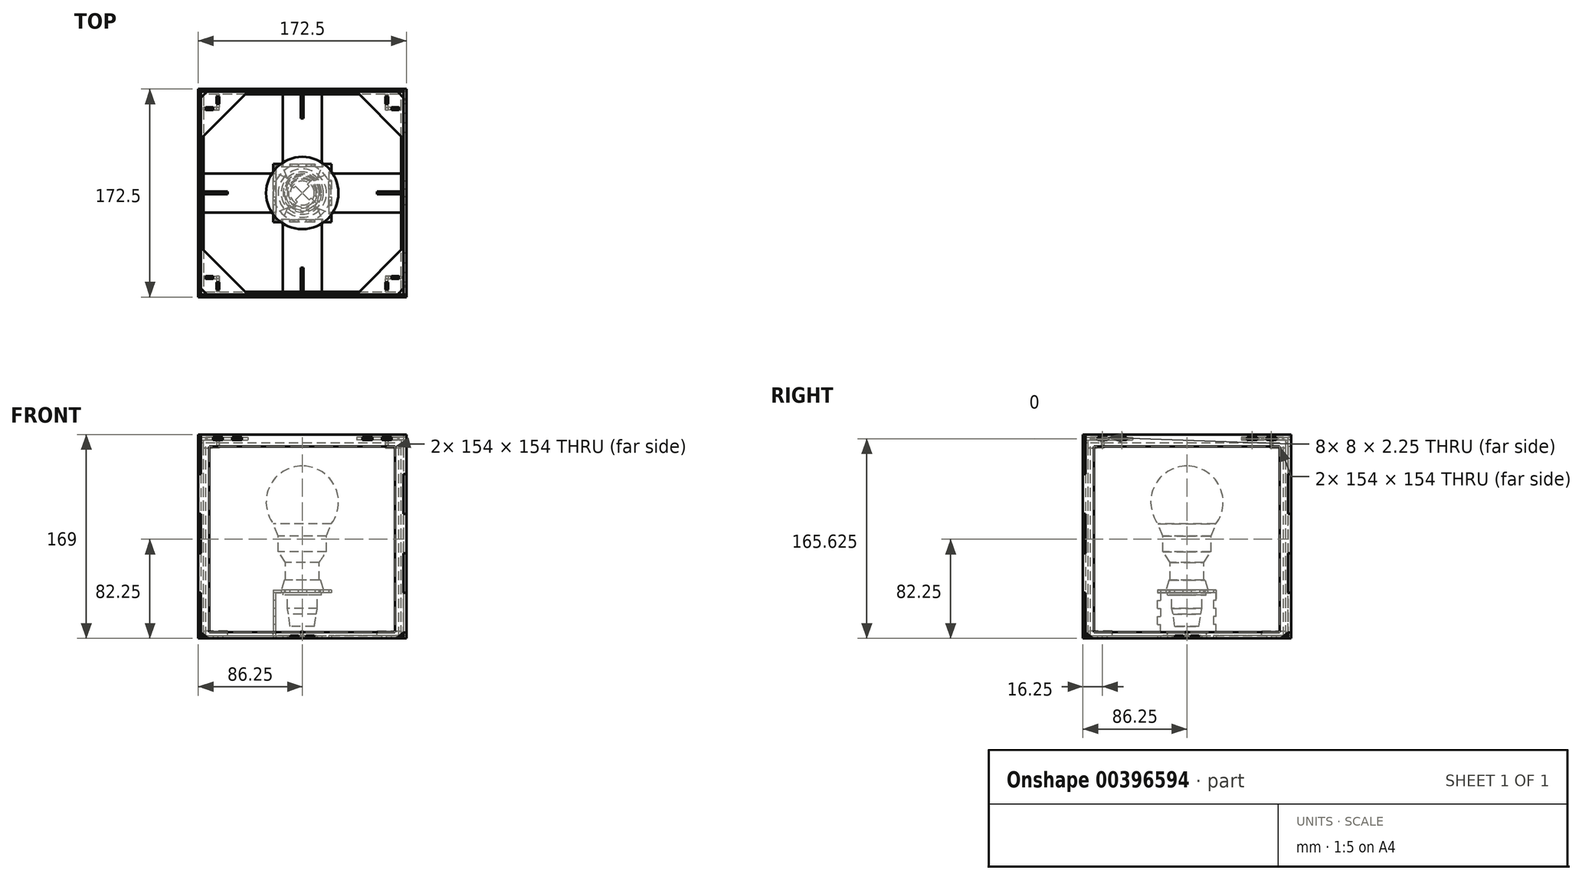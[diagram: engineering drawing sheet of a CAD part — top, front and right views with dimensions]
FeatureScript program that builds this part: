
annotation { "Feature Type Name" : "Feature", "Feature Type Description" : "" }
export const myFeature = defineFeature(function(context is Context, id is Id, definition is map)
    precondition{}
    {
        {
            assignVariable(context, id + "F0", {"name" : "ep", "anyValue" : 2.25});
        }
        {
            var Q0;
            Q0=qCreatedBy(makeId("Front.planeOp"),FACE);
            var sketch = newSketch(context, id + "F1", { "sketchPlane" : qUnion([Q0])});
            skLineSegment(sketch, "E0", {"start": v(0, 10) * mm, "end": v(10, 10) * mm});
            skLineSegment(sketch, "E1", {"start": v(10, 10) * mm, "end": v(11.5, 20) * mm});
            skLineSegment(sketch, "E2", {"start": v(11.5, 20) * mm, "end": v(12.5, 25) * mm});
            skLineSegment(sketch, "E3", {"start": v(12.5, 25) * mm, "end": v(12.5, 36) * mm});
            skLineSegment(sketch, "E4", {"start": v(12.5, 36) * mm, "end": v(16, 36) * mm});
            skLineSegment(sketch, "E5", {"start": v(16, 36) * mm, "end": v(16, 38) * mm});
            skLineSegment(sketch, "E6", {"start": v(16, 38) * mm, "end": v(14, 38) * mm});
            skLineSegment(sketch, "E7", {"start": v(14, 38) * mm, "end": v(14, 40.25) * mm});
            skLineSegment(sketch, "E8", {"start": v(14, 40.25) * mm, "end": v(17.5, 40.25) * mm});
            skLineSegment(sketch, "E9", {"start": v(17.5, 40.25) * mm, "end": v(15, 48.25) * mm});
            skLineSegment(sketch, "E10", {"start": v(15, 48.25) * mm, "end": v(14, 48.25) * mm});
            skLineSegment(sketch, "E11", {"start": v(14, 48.25) * mm, "end": v(14, 63) * mm});
            skLineSegment(sketch, "E12", {"start": v(14, 63) * mm, "end": v(20, 72) * mm});
            skLineSegment(sketch, "E13", {"start": v(20, 72) * mm, "end": v(20, 85) * mm});
            skLineSegment(sketch, "E14", {"start": v(20, 85) * mm, "end": v(24, 95) * mm});
            skLineSegment(sketch, "E15", {"start": v(0, 10) * mm, "end": v(0, 113) * mm, "construction": true});
            skArc(sketch, "E16", {"start": v(24, 95) * mm, "mid": v(26.83, 126.42) * mm, "end": v(0, 143) * mm});
            skLineSegment(sketch, "E17", {"start": v(0, 143) * mm, "end": v(0, 10) * mm});
            skSolve(sketch);
        }
        {
            var Q0;
            Q0 = qSketchRegion(id + "F1", true);
            var Q1;
            Q1=sQuery(id+"F1.wireOp",EDGE,"E17");
            revolve(context, id + "F2", {"entities" : qUnion([Q0]), "axis" : qUnion([Q1]), "revolveType" : RevolveType.FULL});
        }
        {
            var Q0;
            Q0=makeQuery(id+"F2.opRevolve","SWEPT_FACE",FACE,{"disambiguationData":[OSD([sQuery(id+"F1.wireOp",EDGE,"E6")])]});
            var sketch = newSketch(context, id + "F3", { "sketchPlane" : qUnion([Q0])});
            skCircle(sketch, "E18.0", {"center": v(0, 0) * mm, "radius": 15 * mm});
            skLineSegment(sketch, "E19.top", {"start": v(-17.32, 22) * mm, "end": v(-10.4, 22) * mm});
            skLineSegment(sketch, "E19.left", {"start": v(-17.32, 24.25) * mm, "end": v(-17.32, 22) * mm});
            skLineSegment(sketch, "E19.right", {"start": v(-10.4, 24.25) * mm, "end": v(-10.4, 22) * mm});
            skLineSegment(sketch, "E20.1.0.0", {"start": v(3.46, 24.25) * mm, "end": v(3.46, 22) * mm});
            skLineSegment(sketch, "E20.1.0.1", {"start": v(-3.46, 22) * mm, "end": v(3.46, 22) * mm});
            skLineSegment(sketch, "E20.1.0.3", {"start": v(-3.46, 24.25) * mm, "end": v(-3.46, 22) * mm});
            skLineSegment(sketch, "E20.2.0.0", {"start": v(17.32, 24.25) * mm, "end": v(17.32, 22) * mm});
            skLineSegment(sketch, "E20.2.0.1", {"start": v(10.4, 22) * mm, "end": v(17.32, 22) * mm});
            skLineSegment(sketch, "E20.2.0.3", {"start": v(10.4, 24.25) * mm, "end": v(10.4, 22) * mm});
            skLineSegment(sketch, "E21", {"start": v(-24.25, 24.25) * mm, "end": v(-17.32, 24.25) * mm});
            skLineSegment(sketch, "E22", {"start": v(-10.4, 24.25) * mm, "end": v(-3.46, 24.25) * mm});
            skLineSegment(sketch, "E23", {"start": v(3.46, 24.25) * mm, "end": v(10.4, 24.25) * mm});
            skLineSegment(sketch, "E24", {"start": v(17.32, 24.25) * mm, "end": v(24.25, 24.25) * mm});
            skLineSegment(sketch, "E25.1.0", {"start": v(-24.25, -3.46) * mm, "end": v(-22, -3.46) * mm});
            skLineSegment(sketch, "E25.1.1", {"start": v(-22, -3.46) * mm, "end": v(-22, 3.46) * mm});
            skLineSegment(sketch, "E25.1.2", {"start": v(-24.25, 17.32) * mm, "end": v(-22, 17.32) * mm});
            skLineSegment(sketch, "E25.1.3", {"start": v(-24.25, 3.46) * mm, "end": v(-24.25, 10.4) * mm});
            skLineSegment(sketch, "E25.1.4", {"start": v(-24.25, 3.46) * mm, "end": v(-22, 3.46) * mm});
            skLineSegment(sketch, "E25.1.5", {"start": v(-24.25, -10.4) * mm, "end": v(-24.25, -3.46) * mm});
            skLineSegment(sketch, "E25.1.6", {"start": v(-24.25, -10.4) * mm, "end": v(-22, -10.4) * mm});
            skLineSegment(sketch, "E25.1.7", {"start": v(-24.25, -24.25) * mm, "end": v(-24.25, -17.32) * mm});
            skLineSegment(sketch, "E25.1.8", {"start": v(-24.25, 10.4) * mm, "end": v(-22, 10.4) * mm});
            skLineSegment(sketch, "E25.1.9", {"start": v(-24.25, -17.32) * mm, "end": v(-22, -17.32) * mm});
            skLineSegment(sketch, "E25.1.10", {"start": v(-22, 10.4) * mm, "end": v(-22, 17.32) * mm});
            skLineSegment(sketch, "E25.1.11", {"start": v(-24.25, 17.32) * mm, "end": v(-24.25, 24.25) * mm});
            skLineSegment(sketch, "E25.1.12", {"start": v(-22, -17.32) * mm, "end": v(-22, -10.4) * mm});
            skLineSegment(sketch, "E25.2.0", {"start": v(3.46, -24.25) * mm, "end": v(3.46, -22) * mm});
            skLineSegment(sketch, "E25.2.1", {"start": v(3.46, -22) * mm, "end": v(-3.46, -22) * mm});
            skLineSegment(sketch, "E25.2.2", {"start": v(-17.32, -24.25) * mm, "end": v(-17.32, -22) * mm});
            skLineSegment(sketch, "E25.2.3", {"start": v(-3.46, -24.25) * mm, "end": v(-10.4, -24.25) * mm});
            skLineSegment(sketch, "E25.2.4", {"start": v(-3.46, -24.25) * mm, "end": v(-3.46, -22) * mm});
            skLineSegment(sketch, "E25.2.5", {"start": v(10.4, -24.25) * mm, "end": v(3.46, -24.25) * mm});
            skLineSegment(sketch, "E25.2.6", {"start": v(10.4, -24.25) * mm, "end": v(10.4, -22) * mm});
            skLineSegment(sketch, "E25.2.7", {"start": v(24.25, -24.25) * mm, "end": v(17.32, -24.25) * mm});
            skLineSegment(sketch, "E25.2.8", {"start": v(-10.4, -24.25) * mm, "end": v(-10.4, -22) * mm});
            skLineSegment(sketch, "E25.2.9", {"start": v(17.32, -24.25) * mm, "end": v(17.32, -22) * mm});
            skLineSegment(sketch, "E25.2.10", {"start": v(-10.4, -22) * mm, "end": v(-17.32, -22) * mm});
            skLineSegment(sketch, "E25.2.11", {"start": v(-17.32, -24.25) * mm, "end": v(-24.25, -24.25) * mm});
            skLineSegment(sketch, "E25.2.12", {"start": v(17.32, -22) * mm, "end": v(10.4, -22) * mm});
            skLineSegment(sketch, "E25.3.0", {"start": v(24.25, 3.46) * mm, "end": v(22, 3.46) * mm});
            skLineSegment(sketch, "E25.3.1", {"start": v(22, 3.46) * mm, "end": v(22, -3.46) * mm});
            skLineSegment(sketch, "E25.3.2", {"start": v(24.25, -17.32) * mm, "end": v(22, -17.32) * mm});
            skLineSegment(sketch, "E25.3.3", {"start": v(24.25, -3.46) * mm, "end": v(24.25, -10.4) * mm});
            skLineSegment(sketch, "E25.3.4", {"start": v(24.25, -3.46) * mm, "end": v(22, -3.46) * mm});
            skLineSegment(sketch, "E25.3.5", {"start": v(24.25, 10.4) * mm, "end": v(24.25, 3.46) * mm});
            skLineSegment(sketch, "E25.3.6", {"start": v(24.25, 10.4) * mm, "end": v(22, 10.4) * mm});
            skLineSegment(sketch, "E25.3.7", {"start": v(24.25, 24.25) * mm, "end": v(24.25, 17.32) * mm});
            skLineSegment(sketch, "E25.3.8", {"start": v(24.25, -10.4) * mm, "end": v(22, -10.4) * mm});
            skLineSegment(sketch, "E25.3.9", {"start": v(24.25, 17.32) * mm, "end": v(22, 17.32) * mm});
            skLineSegment(sketch, "E25.3.10", {"start": v(22, -10.4) * mm, "end": v(22, -17.32) * mm});
            skLineSegment(sketch, "E25.3.11", {"start": v(24.25, -17.32) * mm, "end": v(24.25, -24.25) * mm});
            skLineSegment(sketch, "E25.3.12", {"start": v(22, 17.32) * mm, "end": v(22, 10.4) * mm});
            skSolve(sketch);
        }
        {
            var Q0;
            Q0=makeQuery(id+"F3.imprint","IMPRINT",FACE,{"disambiguationData":[TD([[makeQuery(id+"F3.imprint","IMPRINT",EDGE,{"derivedFrom":sQuery(id+"F3.wireOp",EDGE,"E19.top")}),-1.0]])]});
            var Q1;
            Q1=makeQuery(id+"F3.imprint","IMPRINT",FACE,{"disambiguationData":[TD([[makeQuery(id+"F3.imprint","IMPRINT",EDGE,{"derivedFrom":sQuery(id+"F3.wireOp",EDGE,"E18.0")}),-1.0]])]});
            extrude(context, id + "F4", {"entities" : qUnion([Q0, Q1]), "depth" : (getVariable(context, 'ep')) * mm});
        }
        {
            var Q0;
            Q0=makeQuery(id+"F4.opExtrude","CAP_FACE",FACE,{"disambiguationData":[OSD([sQuery(id+"F3.wireOp",EDGE,"E18.0"),sQuery(id+"F3.wireOp",EDGE,"E19.top"),sQuery(id+"F3.wireOp",EDGE,"E19.left"),sQuery(id+"F3.wireOp",EDGE,"E19.right"),sQuery(id+"F3.wireOp",EDGE,"E20.1.0.0"),sQuery(id+"F3.wireOp",EDGE,"E20.1.0.1"),sQuery(id+"F3.wireOp",EDGE,"E20.1.0.3"),sQuery(id+"F3.wireOp",EDGE,"E20.2.0.0"),sQuery(id+"F3.wireOp",EDGE,"E20.2.0.1"),sQuery(id+"F3.wireOp",EDGE,"E20.2.0.3"),sQuery(id+"F3.wireOp",EDGE,"E21"),sQuery(id+"F3.wireOp",EDGE,"E22"),sQuery(id+"F3.wireOp",EDGE,"E23"),sQuery(id+"F3.wireOp",EDGE,"E24"),sQuery(id+"F3.wireOp",EDGE,"E25.1.0"),sQuery(id+"F3.wireOp",EDGE,"E25.1.1"),sQuery(id+"F3.wireOp",EDGE,"E25.1.2"),sQuery(id+"F3.wireOp",EDGE,"E25.1.3"),sQuery(id+"F3.wireOp",EDGE,"E25.1.4"),sQuery(id+"F3.wireOp",EDGE,"E25.1.5"),sQuery(id+"F3.wireOp",EDGE,"E25.1.6"),sQuery(id+"F3.wireOp",EDGE,"E25.1.7"),sQuery(id+"F3.wireOp",EDGE,"E25.1.8"),sQuery(id+"F3.wireOp",EDGE,"E25.1.9"),sQuery(id+"F3.wireOp",EDGE,"E25.1.10"),sQuery(id+"F3.wireOp",EDGE,"E25.1.11"),sQuery(id+"F3.wireOp",EDGE,"E25.1.12"),sQuery(id+"F3.wireOp",EDGE,"E25.2.0"),sQuery(id+"F3.wireOp",EDGE,"E25.2.1"),sQuery(id+"F3.wireOp",EDGE,"E25.2.2"),sQuery(id+"F3.wireOp",EDGE,"E25.2.3"),sQuery(id+"F3.wireOp",EDGE,"E25.2.4"),sQuery(id+"F3.wireOp",EDGE,"E25.2.5"),sQuery(id+"F3.wireOp",EDGE,"E25.2.6"),sQuery(id+"F3.wireOp",EDGE,"E25.2.7"),sQuery(id+"F3.wireOp",EDGE,"E25.2.8"),sQuery(id+"F3.wireOp",EDGE,"E25.2.9"),sQuery(id+"F3.wireOp",EDGE,"E25.2.10"),sQuery(id+"F3.wireOp",EDGE,"E25.2.11"),sQuery(id+"F3.wireOp",EDGE,"E25.2.12"),sQuery(id+"F3.wireOp",EDGE,"E25.3.0"),sQuery(id+"F3.wireOp",EDGE,"E25.3.1"),sQuery(id+"F3.wireOp",EDGE,"E25.3.2"),sQuery(id+"F3.wireOp",EDGE,"E25.3.3"),sQuery(id+"F3.wireOp",EDGE,"E25.3.4"),sQuery(id+"F3.wireOp",EDGE,"E25.3.5"),sQuery(id+"F3.wireOp",EDGE,"E25.3.6"),sQuery(id+"F3.wireOp",EDGE,"E25.3.7"),sQuery(id+"F3.wireOp",EDGE,"E25.3.8"),sQuery(id+"F3.wireOp",EDGE,"E25.3.9"),sQuery(id+"F3.wireOp",EDGE,"E25.3.10"),sQuery(id+"F3.wireOp",EDGE,"E25.3.11"),sQuery(id+"F3.wireOp",EDGE,"E25.3.12")])],"isStart":true});
            var sketch = newSketch(context, id + "F5", { "sketchPlane" : qUnion([Q0])});
            skLineSegment(sketch, "E26.left", {"start": v(-24.25, 24.25) * mm, "end": v(-24.25, -24.25) * mm});
            skLineSegment(sketch, "E26.right", {"start": v(24.25, 24.25) * mm, "end": v(24.25, -24.25) * mm});
            skLineSegment(sketch, "E27", {"start": v(22, 24.25) * mm, "end": v(22, -24.25) * mm});
            skLineSegment(sketch, "E28", {"start": v(22, -24.25) * mm, "end": v(24.25, -24.25) * mm});
            skLineSegment(sketch, "E29", {"start": v(22, 24.25) * mm, "end": v(24.25, 24.25) * mm});
            skLineSegment(sketch, "E30", {"start": v(-22, 24.25) * mm, "end": v(-22, -24.25) * mm});
            skLineSegment(sketch, "E31", {"start": v(-22, -24.25) * mm, "end": v(-24.25, -24.25) * mm});
            skLineSegment(sketch, "E32", {"start": v(-24.25, 24.25) * mm, "end": v(-22, 24.25) * mm});
            skSolve(sketch);
        }
        {
            var Q0;
            {var subQ0=sQuery(id+"F5.wireOp",EDGE,"E32");Q0=makeQuery(id+"F5.imprint","IMPRINT",FACE,{"disambiguationData":[TD([[makeQuery(id+"F5.imprint","IMPRINT",EDGE,{"derivedFrom":subQ0}),1.0]])]});}
            var Q1;
            {var subQ1=makeQuery(id+"F4.opExtrude","CAP_EDGE",EDGE,{"disambiguationData":[OSD([sQuery(id+"F3.wireOp",EDGE,"E25.1.6")])],"isStart":true});Q1=makeQuery(id+"F5.imprint","IMPRINT",FACE,{"disambiguationData":[TD([[makeQuery(id+"F5.imprint","IMPRINT",EDGE,{"derivedFrom":subQ1}),1.0]])]});}
            var Q2;
            {var subQ1=makeQuery(id+"F4.opExtrude","CAP_EDGE",EDGE,{"disambiguationData":[OSD([sQuery(id+"F3.wireOp",EDGE,"E25.1.0")])],"isStart":true});Q2=makeQuery(id+"F5.imprint","IMPRINT",FACE,{"disambiguationData":[TD([[makeQuery(id+"F5.imprint","IMPRINT",EDGE,{"derivedFrom":subQ1}),1.0]])]});}
            var Q3;
            {var subQ1=makeQuery(id+"F4.opExtrude","CAP_EDGE",EDGE,{"disambiguationData":[OSD([sQuery(id+"F3.wireOp",EDGE,"E25.1.0")])],"isStart":true});Q3=makeQuery(id+"F5.imprint","IMPRINT",FACE,{"disambiguationData":[TD([[makeQuery(id+"F5.imprint","IMPRINT",EDGE,{"derivedFrom":subQ1}),-1.0]])]});}
            var Q4;
            {var subQ1=makeQuery(id+"F4.opExtrude","CAP_EDGE",EDGE,{"disambiguationData":[OSD([sQuery(id+"F3.wireOp",EDGE,"E25.1.4")])],"isStart":true});Q4=makeQuery(id+"F5.imprint","IMPRINT",FACE,{"disambiguationData":[TD([[makeQuery(id+"F5.imprint","IMPRINT",EDGE,{"derivedFrom":subQ1}),-1.0]])]});}
            var Q5;
            {var subQ1=makeQuery(id+"F4.opExtrude","CAP_EDGE",EDGE,{"disambiguationData":[OSD([sQuery(id+"F3.wireOp",EDGE,"E25.1.2")])],"isStart":true});Q5=makeQuery(id+"F5.imprint","IMPRINT",FACE,{"disambiguationData":[TD([[makeQuery(id+"F5.imprint","IMPRINT",EDGE,{"derivedFrom":subQ1}),1.0]])]});}
            var Q6;
            {var subQ0=sQuery(id+"F5.wireOp",EDGE,"E31");Q6=makeQuery(id+"F5.imprint","IMPRINT",FACE,{"disambiguationData":[TD([[makeQuery(id+"F5.imprint","IMPRINT",EDGE,{"derivedFrom":subQ0}),1.0]])]});}
            var Q7;
            Q7=qCreatedBy(makeId("Top.planeOp"),FACE);
            extrude(context, id + "F6", {"entities" : qUnion([Q0, Q1, Q2, Q3, Q4, Q5, Q6]), "endBound" : BoundingType.UP_TO_SURFACE, "endBoundEntityFace" : qUnion([Q7]), "depth" : 25 * mm});
        }
        {
            var Q0;
            {var subQ1=makeQuery(id+"F4.opExtrude","CAP_EDGE",EDGE,{"disambiguationData":[OSD([sQuery(id+"F3.wireOp",EDGE,"E25.1.2")])],"isStart":true});Q0=makeQuery(id+"F5.imprint","IMPRINT",FACE,{"disambiguationData":[TD([[makeQuery(id+"F5.imprint","IMPRINT",EDGE,{"derivedFrom":subQ1}),1.0]])]});}
            var Q1;
            {var subQ1=makeQuery(id+"F4.opExtrude","CAP_EDGE",EDGE,{"disambiguationData":[OSD([sQuery(id+"F3.wireOp",EDGE,"E25.1.0")])],"isStart":true});Q1=makeQuery(id+"F5.imprint","IMPRINT",FACE,{"disambiguationData":[TD([[makeQuery(id+"F5.imprint","IMPRINT",EDGE,{"derivedFrom":subQ1}),-1.0]])]});}
            var Q2;
            {var subQ1=makeQuery(id+"F4.opExtrude","CAP_EDGE",EDGE,{"disambiguationData":[OSD([sQuery(id+"F3.wireOp",EDGE,"E25.1.6")])],"isStart":true});Q2=makeQuery(id+"F5.imprint","IMPRINT",FACE,{"disambiguationData":[TD([[makeQuery(id+"F5.imprint","IMPRINT",EDGE,{"derivedFrom":subQ1}),1.0]])]});}
            var Q3;
            Q3=makeQuery(id+"F4.opExtrude","CAP_FACE",FACE,{"disambiguationData":[OSD([sQuery(id+"F3.wireOp",EDGE,"E18.0"),sQuery(id+"F3.wireOp",EDGE,"E19.top"),sQuery(id+"F3.wireOp",EDGE,"E19.left"),sQuery(id+"F3.wireOp",EDGE,"E19.right"),sQuery(id+"F3.wireOp",EDGE,"E20.1.0.0"),sQuery(id+"F3.wireOp",EDGE,"E20.1.0.1"),sQuery(id+"F3.wireOp",EDGE,"E20.1.0.3"),sQuery(id+"F3.wireOp",EDGE,"E20.2.0.0"),sQuery(id+"F3.wireOp",EDGE,"E20.2.0.1"),sQuery(id+"F3.wireOp",EDGE,"E20.2.0.3"),sQuery(id+"F3.wireOp",EDGE,"E21"),sQuery(id+"F3.wireOp",EDGE,"E22"),sQuery(id+"F3.wireOp",EDGE,"E23"),sQuery(id+"F3.wireOp",EDGE,"E24"),sQuery(id+"F3.wireOp",EDGE,"E25.1.0"),sQuery(id+"F3.wireOp",EDGE,"E25.1.1"),sQuery(id+"F3.wireOp",EDGE,"E25.1.2"),sQuery(id+"F3.wireOp",EDGE,"E25.1.3"),sQuery(id+"F3.wireOp",EDGE,"E25.1.4"),sQuery(id+"F3.wireOp",EDGE,"E25.1.5"),sQuery(id+"F3.wireOp",EDGE,"E25.1.6"),sQuery(id+"F3.wireOp",EDGE,"E25.1.7"),sQuery(id+"F3.wireOp",EDGE,"E25.1.8"),sQuery(id+"F3.wireOp",EDGE,"E25.1.9"),sQuery(id+"F3.wireOp",EDGE,"E25.1.10"),sQuery(id+"F3.wireOp",EDGE,"E25.1.11"),sQuery(id+"F3.wireOp",EDGE,"E25.1.12"),sQuery(id+"F3.wireOp",EDGE,"E25.2.0"),sQuery(id+"F3.wireOp",EDGE,"E25.2.1"),sQuery(id+"F3.wireOp",EDGE,"E25.2.2"),sQuery(id+"F3.wireOp",EDGE,"E25.2.3"),sQuery(id+"F3.wireOp",EDGE,"E25.2.4"),sQuery(id+"F3.wireOp",EDGE,"E25.2.5"),sQuery(id+"F3.wireOp",EDGE,"E25.2.6"),sQuery(id+"F3.wireOp",EDGE,"E25.2.7"),sQuery(id+"F3.wireOp",EDGE,"E25.2.8"),sQuery(id+"F3.wireOp",EDGE,"E25.2.9"),sQuery(id+"F3.wireOp",EDGE,"E25.2.10"),sQuery(id+"F3.wireOp",EDGE,"E25.2.11"),sQuery(id+"F3.wireOp",EDGE,"E25.2.12"),sQuery(id+"F3.wireOp",EDGE,"E25.3.0"),sQuery(id+"F3.wireOp",EDGE,"E25.3.1"),sQuery(id+"F3.wireOp",EDGE,"E25.3.2"),sQuery(id+"F3.wireOp",EDGE,"E25.3.3"),sQuery(id+"F3.wireOp",EDGE,"E25.3.4"),sQuery(id+"F3.wireOp",EDGE,"E25.3.5"),sQuery(id+"F3.wireOp",EDGE,"E25.3.6"),sQuery(id+"F3.wireOp",EDGE,"E25.3.7"),sQuery(id+"F3.wireOp",EDGE,"E25.3.8"),sQuery(id+"F3.wireOp",EDGE,"E25.3.9"),sQuery(id+"F3.wireOp",EDGE,"E25.3.10"),sQuery(id+"F3.wireOp",EDGE,"E25.3.11"),sQuery(id+"F3.wireOp",EDGE,"E25.3.12")])],"isStart":false});
            extrude(context, id + "F7", {"entities" : qUnion([Q0, Q1, Q2]), "operationType" : NewBodyOperationType.ADD, "endBound" : BoundingType.UP_TO_SURFACE, "oppositeDirection" : true, "endBoundEntityFace" : qUnion([Q3]), "depth" : 25 * mm});
        }
        {
            var Q0;
            {var subQ0=sQuery(id+"F5.wireOp",EDGE,"E26.left");Q0=makeQuery(id+"F7.boolean.opBoolean","MERGE",FACE,{"derivedFrom":[makeQuery(id+"F6.opExtrude","SWEPT_FACE",FACE,{"disambiguationData":[OSD([subQ0])]}),makeQuery(id+"F7.opExtrude","SWEPT_FACE",FACE,{"disambiguationData":[OSD([subQ0]),TDD([makeQuery(id+"F5.imprint","IMPRINT",EDGE,{"disambiguationData":[TD([[makeQuery(id+"F5.imprint","INTERSECT",VERTEX,{"derivedFrom":[makeQuery(id+"F4.opExtrude","CAP_EDGE",EDGE,{"disambiguationData":[OSD([sQuery(id+"F3.wireOp",EDGE,"E25.1.6")])],"isStart":true}),subQ0]}),1.0]])],"derivedFrom":subQ0})])]}),makeQuery(id+"F7.opExtrude","SWEPT_FACE",FACE,{"disambiguationData":[OSD([subQ0]),TDD([makeQuery(id+"F5.imprint","IMPRINT",EDGE,{"disambiguationData":[TD([[makeQuery(id+"F5.imprint","INTERSECT",VERTEX,{"derivedFrom":[makeQuery(id+"F4.opExtrude","CAP_EDGE",EDGE,{"disambiguationData":[OSD([sQuery(id+"F3.wireOp",EDGE,"E25.1.0")])],"isStart":true}),subQ0]}),-1.0]])],"derivedFrom":subQ0})])]}),makeQuery(id+"F7.opExtrude","SWEPT_FACE",FACE,{"disambiguationData":[OSD([subQ0]),TDD([makeQuery(id+"F5.imprint","IMPRINT",EDGE,{"disambiguationData":[TD([[makeQuery(id+"F5.imprint","INTERSECT",VERTEX,{"derivedFrom":[makeQuery(id+"F4.opExtrude","CAP_EDGE",EDGE,{"disambiguationData":[OSD([sQuery(id+"F3.wireOp",EDGE,"E25.1.2")])],"isStart":true}),subQ0]}),1.0]])],"derivedFrom":subQ0})])]})]});}
            var sketch = newSketch(context, id + "F8", { "sketchPlane" : qUnion([Q0])});
            skLineSegment(sketch, "E33.bottom", {"start": v(-24.25, 0) * mm, "end": v(-9.75, 0) * mm});
            skLineSegment(sketch, "E33.top", {"start": v(-24.25, 5) * mm, "end": v(-16.25, 5) * mm});
            skLineSegment(sketch, "E33.left", {"start": v(-24.25, 0) * mm, "end": v(-24.25, 5) * mm});
            skLineSegment(sketch, "E33.right", {"start": v(-16.25, 2.25) * mm, "end": v(-16.25, 5) * mm});
            skLineSegment(sketch, "E34.bottom", {"start": v(24.25, 0) * mm, "end": v(9.75, 0) * mm});
            skLineSegment(sketch, "E34.top", {"start": v(22, 5) * mm, "end": v(16.25, 5) * mm});
            skLineSegment(sketch, "E34.left", {"start": v(24.25, 0) * mm, "end": v(24.25, 5) * mm});
            skLineSegment(sketch, "E34.right", {"start": v(16.25, 2.25) * mm, "end": v(16.25, 5) * mm});
            skLineSegment(sketch, "E35.bottom", {"start": v(-24.25, 31.4) * mm, "end": v(-22, 31.4) * mm});
            skLineSegment(sketch, "E35.top", {"start": v(-24.25, 24.8) * mm, "end": v(-22, 24.8) * mm});
            skLineSegment(sketch, "E35.left", {"start": v(-24.25, 31.4) * mm, "end": v(-24.25, 24.8) * mm});
            skLineSegment(sketch, "E35.right", {"start": v(-22, 31.4) * mm, "end": v(-22, 24.8) * mm});
            skLineSegment(sketch, "E36.bottom", {"start": v(-24.25, 18.2) * mm, "end": v(-22, 18.2) * mm});
            skLineSegment(sketch, "E36.top", {"start": v(-24.25, 11.6) * mm, "end": v(-22, 11.6) * mm});
            skLineSegment(sketch, "E36.left", {"start": v(-24.25, 18.2) * mm, "end": v(-24.25, 11.6) * mm});
            skLineSegment(sketch, "E36.right", {"start": v(-22, 18.2) * mm, "end": v(-22, 11.6) * mm});
            skLineSegment(sketch, "E37", {"start": v(-24.25, 38) * mm, "end": v(-24.25, 31.4) * mm, "construction": true});
            skLineSegment(sketch, "E38", {"start": v(-24.25, 24.8) * mm, "end": v(-24.25, 18.2) * mm, "construction": true});
            skLineSegment(sketch, "E39", {"start": v(-24.25, 11.6) * mm, "end": v(-24.25, 5) * mm, "construction": true});
            skLineSegment(sketch, "E40.bottom", {"start": v(24.25, 38) * mm, "end": v(22, 38) * mm});
            skLineSegment(sketch, "E40.top", {"start": v(24.25, 31.4) * mm, "end": v(22, 31.4) * mm});
            skLineSegment(sketch, "E40.left", {"start": v(24.25, 38) * mm, "end": v(24.25, 31.4) * mm});
            skLineSegment(sketch, "E40.right", {"start": v(22, 38) * mm, "end": v(22, 31.4) * mm});
            skLineSegment(sketch, "E41.bottom", {"start": v(24.25, 24.8) * mm, "end": v(22, 24.8) * mm});
            skLineSegment(sketch, "E41.top", {"start": v(24.25, 18.2) * mm, "end": v(22, 18.2) * mm});
            skLineSegment(sketch, "E41.left", {"start": v(24.25, 24.8) * mm, "end": v(24.25, 18.2) * mm});
            skLineSegment(sketch, "E41.right", {"start": v(22, 24.8) * mm, "end": v(22, 18.2) * mm});
            skLineSegment(sketch, "E42.top", {"start": v(24.25, 11.6) * mm, "end": v(22, 11.6) * mm});
            skLineSegment(sketch, "E42.left", {"start": v(24.25, 5) * mm, "end": v(24.25, 11.6) * mm});
            skLineSegment(sketch, "E42.right", {"start": v(22, 5) * mm, "end": v(22, 11.6) * mm});
            skLineSegment(sketch, "E43", {"start": v(24.25, 31.4) * mm, "end": v(24.25, 24.8) * mm, "construction": true});
            skLineSegment(sketch, "E44", {"start": v(24.25, 18.2) * mm, "end": v(24.25, 11.6) * mm, "construction": true});
            skLineSegment(sketch, "E45.bottom", {"start": v(-16.25, 2.25) * mm, "end": v(-9.75, 2.25) * mm});
            skLineSegment(sketch, "E45.right", {"start": v(-9.75, 2.25) * mm, "end": v(-9.75, 0) * mm});
            skLineSegment(sketch, "E46.bottom", {"start": v(-3.25, 0) * mm, "end": v(3.25, 0) * mm});
            skLineSegment(sketch, "E46.top", {"start": v(-3.25, 2.25) * mm, "end": v(3.25, 2.25) * mm});
            skLineSegment(sketch, "E46.left", {"start": v(-3.25, 0) * mm, "end": v(-3.25, 2.25) * mm});
            skLineSegment(sketch, "E46.right", {"start": v(3.25, 0) * mm, "end": v(3.25, 2.25) * mm});
            skLineSegment(sketch, "E47.top", {"start": v(9.75, 2.25) * mm, "end": v(16.25, 2.25) * mm});
            skLineSegment(sketch, "E47.left", {"start": v(9.75, 0) * mm, "end": v(9.75, 2.25) * mm});
            skLineSegment(sketch, "E48", {"start": v(-9.75, 0) * mm, "end": v(-3.25, 0) * mm, "construction": true});
            skLineSegment(sketch, "E49", {"start": v(3.25, 0) * mm, "end": v(9.75, 0) * mm, "construction": true});
            skSolve(sketch);
        }
        {
            var Q0;
            Q0 = qSketchRegion(id + "F8", true);
            extrude(context, id + "F9", {"entities" : qUnion([Q0]), "operationType" : NewBodyOperationType.REMOVE, "endBound" : BoundingType.UP_TO_NEXT, "oppositeDirection" : true, "depth" : 25 * mm});
        }
        {
            var Q0;
            Q0=qCreatedBy(makeId("Right.planeOp"),FACE);
            cPlane(context, id + "F10", {"entities" : qUnion([Q0]), "cplaneType" : CPlaneType.OFFSET, "offset" : ((172.5) / 2 - 2 - getVariable(context, 'ep')) * mm, "oppositeDirection" : true, "width" : 150 * mm, "height" : 150 * mm});
        }
        {
            var Q0;
            Q0=qCreatedBy(id+"F10.planeOp",FACE);
            var sketch = newSketch(context, id + "F11", { "sketchPlane" : qUnion([Q0])});
            skLineSegment(sketch, "E50.bottom", {"start": v(80, 2.25) * mm, "end": v(-80, 2.25) * mm});
            skLineSegment(sketch, "E50.top", {"start": v(80, 162.25) * mm, "end": v(-80, 162.25) * mm});
            skLineSegment(sketch, "E50.left", {"start": v(80, 2.25) * mm, "end": v(80, 162.25) * mm});
            skLineSegment(sketch, "E50.right", {"start": v(-80, 2.25) * mm, "end": v(-80, 162.25) * mm});
            skPoint(sketch, "E50.middle", {"position": v(0, 82.25) * mm});
            skSolve(sketch);
        }
        {
            var Q0;
            Q0=makeQuery(id+"F11.imprint","IMPRINT",FACE,{"disambiguationData":[TD([[makeQuery(id+"F11.imprint","IMPRINT",EDGE,{"derivedFrom":sQuery(id+"F11.wireOp",EDGE,"E50.bottom")}),-1.0]])]});
            extrude(context, id + "F12", {"entities" : qUnion([Q0]), "oppositeDirection" : true, "depth" : 2 * mm});
        }
        {
            var Q0;
            Q0=makeQuery(id+"F12.opExtrude","CAP_FACE",FACE,{"disambiguationData":[OSD([sQuery(id+"F11.wireOp",EDGE,"E50.bottom"),sQuery(id+"F11.wireOp",EDGE,"E50.top"),sQuery(id+"F11.wireOp",EDGE,"E50.left"),sQuery(id+"F11.wireOp",EDGE,"E50.right")])],"isStart":false});
            var sketch = newSketch(context, id + "F13", { "sketchPlane" : qUnion([Q0])});
            skLineSegment(sketch, "E51.0", {"start": v(-77, 159.25) * mm, "end": v(-77, 5.25) * mm});
            skLineSegment(sketch, "E51.1", {"start": v(77, 159.25) * mm, "end": v(-77, 159.25) * mm});
            skLineSegment(sketch, "E51.2", {"start": v(77, 5.25) * mm, "end": v(77, 159.25) * mm});
            skLineSegment(sketch, "E51.3", {"start": v(-77, 5.25) * mm, "end": v(77, 5.25) * mm});
            skLineSegment(sketch, "E52.0", {"start": v(-86.25, 136.2) * mm, "end": v(-86.25, 103.4) * mm});
            skLineSegment(sketch, "E52.1", {"start": v(86.25, 169) * mm, "end": v(-84, 169) * mm});
            skLineSegment(sketch, "E52.2", {"start": v(86.25, 5) * mm, "end": v(86.25, 37.8) * mm});
            skLineSegment(sketch, "E52.3", {"start": v(-78, 0) * mm, "end": v(-9.75, 0) * mm});
            skLineSegment(sketch, "E53", {"start": v(-84, 5) * mm, "end": v(-78, 0) * mm});
            skLineSegment(sketch, "E54.top", {"start": v(-86.25, 136.2) * mm, "end": v(-84, 136.2) * mm});
            skLineSegment(sketch, "E54.right", {"start": v(-84, 169) * mm, "end": v(-84, 136.2) * mm});
            skLineSegment(sketch, "E55.bottom", {"start": v(-86.25, 103.4) * mm, "end": v(-84, 103.4) * mm});
            skLineSegment(sketch, "E55.top", {"start": v(-86.25, 70.6) * mm, "end": v(-84, 70.6) * mm});
            skLineSegment(sketch, "E55.right", {"start": v(-84, 103.4) * mm, "end": v(-84, 70.6) * mm});
            skLineSegment(sketch, "E56.bottom", {"start": v(-86.25, 37.8) * mm, "end": v(-84, 37.8) * mm});
            skLineSegment(sketch, "E56.right", {"start": v(-84, 37.8) * mm, "end": v(-84, 5) * mm});
            skLineSegment(sketch, "E57.trimOffspring", {"start": v(-86.25, 70.6) * mm, "end": v(-86.25, 37.8) * mm});
            skLineSegment(sketch, "E58.bottom", {"start": v(86.25, 136.2) * mm, "end": v(84, 136.2) * mm});
            skLineSegment(sketch, "E58.top", {"start": v(86.25, 103.4) * mm, "end": v(84, 103.4) * mm});
            skLineSegment(sketch, "E58.right", {"start": v(84, 136.2) * mm, "end": v(84, 103.4) * mm});
            skLineSegment(sketch, "E59.bottom", {"start": v(86.25, 70.6) * mm, "end": v(84, 70.6) * mm});
            skLineSegment(sketch, "E59.top", {"start": v(86.25, 37.8) * mm, "end": v(84, 37.8) * mm});
            skLineSegment(sketch, "E59.right", {"start": v(84, 70.6) * mm, "end": v(84, 37.8) * mm});
            skLineSegment(sketch, "E60.trimOffspring", {"start": v(86.25, 136.2) * mm, "end": v(86.25, 169) * mm});
            skLineSegment(sketch, "E61.trimOffspring", {"start": v(86.25, 70.6) * mm, "end": v(86.25, 103.4) * mm});
            skLineSegment(sketch, "E62", {"start": v(86.25, 5) * mm, "end": v(84, 5) * mm});
            skLineSegment(sketch, "E63", {"start": v(84, 5) * mm, "end": v(78, 0) * mm});
            skLineSegment(sketch, "E64.bottom", {"start": v(-74, 166.75) * mm, "end": v(-66, 166.75) * mm});
            skLineSegment(sketch, "E64.top", {"start": v(-74, 164.5) * mm, "end": v(-66, 164.5) * mm});
            skLineSegment(sketch, "E64.left", {"start": v(-74, 166.75) * mm, "end": v(-74, 164.5) * mm});
            skLineSegment(sketch, "E64.right", {"start": v(-66, 166.75) * mm, "end": v(-66, 164.5) * mm});
            skLineSegment(sketch, "E65.bottom", {"start": v(-58, 166.75) * mm, "end": v(-50, 166.75) * mm});
            skLineSegment(sketch, "E65.top", {"start": v(-58, 164.5) * mm, "end": v(-50, 164.5) * mm});
            skLineSegment(sketch, "E65.left", {"start": v(-58, 166.75) * mm, "end": v(-58, 164.5) * mm});
            skLineSegment(sketch, "E65.right", {"start": v(-50, 166.75) * mm, "end": v(-50, 164.5) * mm});
            skLineSegment(sketch, "E66", {"start": v(-66, 166.75) * mm, "end": v(-58, 166.75) * mm, "construction": true});
            skLineSegment(sketch, "E67.MirrorCS", {"start": v(74, 166.75) * mm, "end": v(74, 164.5) * mm});
            skLineSegment(sketch, "E68.MirrorCS", {"start": v(74, 166.75) * mm, "end": v(66, 166.75) * mm});
            skLineSegment(sketch, "E69.MirrorCS", {"start": v(66, 166.75) * mm, "end": v(66, 164.5) * mm});
            skLineSegment(sketch, "E70.MirrorCS", {"start": v(74, 164.5) * mm, "end": v(66, 164.5) * mm});
            skLineSegment(sketch, "E71.MirrorCS", {"start": v(58, 166.75) * mm, "end": v(58, 164.5) * mm});
            skLineSegment(sketch, "E72.MirrorCS", {"start": v(58, 166.75) * mm, "end": v(50, 166.75) * mm});
            skLineSegment(sketch, "E73.MirrorCS", {"start": v(58, 164.5) * mm, "end": v(50, 164.5) * mm});
            skLineSegment(sketch, "E74.MirrorCS", {"start": v(50, 166.75) * mm, "end": v(50, 164.5) * mm});
            skLineSegment(sketch, "E75.0", {"start": v(-9.75, 2.25) * mm, "end": v(-9.75, 0) * mm});
            skLineSegment(sketch, "E76.0", {"start": v(-3.25, 0) * mm, "end": v(-3.25, 2.25) * mm});
            skLineSegment(sketch, "E77.0", {"start": v(3.25, 0) * mm, "end": v(3.25, 2.25) * mm});
            skLineSegment(sketch, "E78.0", {"start": v(9.75, 0) * mm, "end": v(9.75, 2.25) * mm});
            skLineSegment(sketch, "E79", {"start": v(-9.75, 2.25) * mm, "end": v(-3.25, 2.25) * mm});
            skLineSegment(sketch, "E80", {"start": v(3.25, 2.25) * mm, "end": v(9.75, 2.25) * mm});
            skLineSegment(sketch, "E81.trimOffspring", {"start": v(-3.25, 0) * mm, "end": v(3.25, 0) * mm});
            skLineSegment(sketch, "E82.trimOffspring", {"start": v(9.75, 0) * mm, "end": v(78, 0) * mm});
            skSolve(sketch);
        }
        {
            var Q0;
            Q0 = qSketchRegion(id + "F13", true);
            extrude(context, id + "F14", {"entities" : qUnion([Q0]), "depth" : (getVariable(context, 'ep')) * mm});
        }
        {
            var Q0;
            Q0=makeQuery(id+"F14.opExtrude","SWEPT_FACE",FACE,{"disambiguationData":[OSD([sQuery(id+"F13.wireOp",EDGE,"E64.top")])]});
            var sketch = newSketch(context, id + "F15", { "sketchPlane" : qUnion([Q0])});
            skLineSegment(sketch, "E83.0", {"start": v(-86.25, 74) * mm, "end": v(-84, 74) * mm});
            skLineSegment(sketch, "E84.0", {"start": v(-86.25, 74) * mm, "end": v(-86.25, 66) * mm});
            skLineSegment(sketch, "E85.0", {"start": v(-86.25, 66) * mm, "end": v(-84, 66) * mm});
            skLineSegment(sketch, "E86.0", {"start": v(-86.25, 58) * mm, "end": v(-84, 58) * mm});
            skLineSegment(sketch, "E87.0", {"start": v(-86.25, 58) * mm, "end": v(-86.25, 50) * mm});
            skLineSegment(sketch, "E88.0", {"start": v(-86.25, 50) * mm, "end": v(-84, 50) * mm});
            skLineSegment(sketch, "E89", {"start": v(-84, 66) * mm, "end": v(-84, 58) * mm});
            skLineSegment(sketch, "E90", {"start": v(-84, 74) * mm, "end": v(-84, 79) * mm});
            skLineSegment(sketch, "E91", {"start": v(-84, 50) * mm, "end": v(-84, 45) * mm});
            skLineSegment(sketch, "E92", {"start": v(0, 0) * mm, "end": v(-86.25, 86.25) * mm, "construction": true});
            skLineSegment(sketch, "E93.MirrorCS", {"start": v(-74, 84) * mm, "end": v(-79, 84) * mm});
            skLineSegment(sketch, "E94.MirrorCS", {"start": v(-74, 86.25) * mm, "end": v(-74, 84) * mm});
            skLineSegment(sketch, "E95.MirrorCS", {"start": v(-74, 86.25) * mm, "end": v(-66, 86.25) * mm});
            skLineSegment(sketch, "E96.MirrorCS", {"start": v(-66, 86.25) * mm, "end": v(-66, 84) * mm});
            skLineSegment(sketch, "E97.MirrorCS", {"start": v(-66, 84) * mm, "end": v(-58, 84) * mm});
            skLineSegment(sketch, "E98.MirrorCS", {"start": v(-58, 86.25) * mm, "end": v(-58, 84) * mm});
            skLineSegment(sketch, "E99.MirrorCS", {"start": v(-58, 86.25) * mm, "end": v(-50, 86.25) * mm});
            skLineSegment(sketch, "E100.MirrorCS", {"start": v(-50, 86.25) * mm, "end": v(-50, 84) * mm});
            skLineSegment(sketch, "E101.MirrorCS", {"start": v(-50, 84) * mm, "end": v(-45, 84) * mm});
            skLineSegment(sketch, "E102", {"start": v(-45, 84) * mm, "end": v(-84, 45) * mm});
            skLineSegment(sketch, "E103", {"start": v(-79, 84) * mm, "end": v(-84, 79) * mm});
            skLineSegment(sketch, "E104.bottom", {"start": v(-80, 71.13) * mm, "end": v(-74, 71.13) * mm});
            skLineSegment(sketch, "E104.top", {"start": v(-80, 68.88) * mm, "end": v(-74, 68.88) * mm});
            skLineSegment(sketch, "E104.left", {"start": v(-80, 71.13) * mm, "end": v(-80, 68.88) * mm});
            skLineSegment(sketch, "E104.right", {"start": v(-74, 71.13) * mm, "end": v(-74, 68.88) * mm});
            skLineSegment(sketch, "E105", {"start": v(-80, 70) * mm, "end": v(-84, 70) * mm, "construction": true});
            skLineSegment(sketch, "E106.MirrorCS", {"start": v(-71.13, 80) * mm, "end": v(-71.13, 74) * mm});
            skLineSegment(sketch, "E107.MirrorCS", {"start": v(-71.13, 74) * mm, "end": v(-68.88, 74) * mm});
            skLineSegment(sketch, "E108.MirrorCS", {"start": v(-68.88, 80) * mm, "end": v(-68.88, 74) * mm});
            skLineSegment(sketch, "E109.MirrorCS", {"start": v(-71.13, 80) * mm, "end": v(-68.88, 80) * mm});
            skSolve(sketch);
        }
        {
            var Q0;
            Q0 = qSketchRegion(id + "F15", true);
            var Q1;
            Q1=makeQuery(id+"F14.opExtrude","SWEPT_FACE",FACE,{"disambiguationData":[OSD([sQuery(id+"F13.wireOp",EDGE,"E64.bottom")])]});
            extrude(context, id + "F16", {"entities" : qUnion([Q0]), "endBound" : BoundingType.UP_TO_SURFACE, "endBoundEntityFace" : qUnion([Q1]), "depth" : 25 * mm});
        }
        {
            var Q0;
            Q0=makeQuery(id+"F16.opExtrude","SWEPT_FACE",FACE,{"disambiguationData":[OSD([sQuery(id+"F15.wireOp",EDGE,"E104.bottom")])]});
            var sketch = newSketch(context, id + "F17", { "sketchPlane" : qUnion([Q0])});
            skLineSegment(sketch, "E110.0", {"start": v(-80, 166.75) * mm, "end": v(-80, 164.5) * mm});
            skLineSegment(sketch, "E111.0", {"start": v(-80, 166.75) * mm, "end": v(-74, 166.75) * mm});
            skLineSegment(sketch, "E112.0", {"start": v(-74, 166.75) * mm, "end": v(-74, 164.5) * mm});
            skLineSegment(sketch, "E113", {"start": v(-80, 164.5) * mm, "end": v(-82, 164.5) * mm});
            skLineSegment(sketch, "E114", {"start": v(-82, 164.5) * mm, "end": v(-82, 157.75) * mm});
            skLineSegment(sketch, "E115", {"start": v(-82, 157.75) * mm, "end": v(-68.88, 157.75) * mm});
            skLineSegment(sketch, "E116", {"start": v(-68.88, 157.75) * mm, "end": v(-68.88, 160) * mm});
            skLineSegment(sketch, "E117", {"start": v(-68.88, 160) * mm, "end": v(-71.13, 160) * mm});
            skLineSegment(sketch, "E118", {"start": v(-71.13, 160) * mm, "end": v(-71.13, 162.25) * mm});
            skLineSegment(sketch, "E119", {"start": v(-71.13, 162.25) * mm, "end": v(-68.88, 162.25) * mm});
            skLineSegment(sketch, "E120", {"start": v(-68.88, 162.25) * mm, "end": v(-68.88, 164.5) * mm});
            skLineSegment(sketch, "E121", {"start": v(-68.88, 164.5) * mm, "end": v(-74, 164.5) * mm});
            skSolve(sketch);
        }
        {
            var Q0;
            Q0 = qSketchRegion(id + "F17", true);
            var Q1;
            Q1=makeQuery(id+"F16.opExtrude","SWEPT_FACE",FACE,{"disambiguationData":[OSD([sQuery(id+"F15.wireOp",EDGE,"E104.top")])]});
            extrude(context, id + "F18", {"entities" : qUnion([Q0]), "endBound" : BoundingType.UP_TO_SURFACE, "endBoundEntityFace" : qUnion([Q1]), "depth" : 25 * mm});
        }
        {
            var Q0;
            Q0=makeQuery(id+"F16.opExtrude","SWEPT_FACE",FACE,{"disambiguationData":[OSD([sQuery(id+"F15.wireOp",EDGE,"E106.MirrorCS")])]});
            var sketch = newSketch(context, id + "F19", { "sketchPlane" : qUnion([Q0])});
            skLineSegment(sketch, "E122.0", {"start": v(80, 166.75) * mm, "end": v(80, 164.5) * mm});
            skLineSegment(sketch, "E123.0", {"start": v(80, 166.75) * mm, "end": v(74, 166.75) * mm});
            skLineSegment(sketch, "E124.0", {"start": v(74, 166.75) * mm, "end": v(74, 164.5) * mm});
            skLineSegment(sketch, "E125.0", {"start": v(71.13, 162.25) * mm, "end": v(71.13, 164.5) * mm});
            skLineSegment(sketch, "E126.0", {"start": v(68.87, 162.25) * mm, "end": v(71.12, 162.25) * mm});
            skLineSegment(sketch, "E127.0", {"start": v(68.87, 162.25) * mm, "end": v(68.87, 160) * mm});
            skLineSegment(sketch, "E128.0", {"start": v(68.87, 160) * mm, "end": v(71.12, 160) * mm});
            skLineSegment(sketch, "E129.0", {"start": v(71.13, 157.75) * mm, "end": v(71.13, 160) * mm});
            skLineSegment(sketch, "E130", {"start": v(74, 164.5) * mm, "end": v(71.13, 164.5) * mm});
            skLineSegment(sketch, "E131", {"start": v(80, 164.5) * mm, "end": v(82, 164.5) * mm});
            skLineSegment(sketch, "E132", {"start": v(82, 164.5) * mm, "end": v(82, 157.75) * mm});
            skLineSegment(sketch, "E133", {"start": v(82, 157.75) * mm, "end": v(71.13, 157.75) * mm});
            skSolve(sketch);
        }
        {
            var Q0;
            Q0 = qSketchRegion(id + "F19", true);
            var Q1;
            Q1=makeQuery(id+"F16.opExtrude","SWEPT_FACE",FACE,{"disambiguationData":[OSD([sQuery(id+"F15.wireOp",EDGE,"E108.MirrorCS")])]});
            extrude(context, id + "F20", {"entities" : qUnion([Q0]), "endBound" : BoundingType.UP_TO_SURFACE, "endBoundEntityFace" : qUnion([Q1]), "depth" : 25 * mm});
        }
        {
            var Q0;
            Q0=qCreatedBy(makeId("Top.planeOp"),FACE);
            var sketch = newSketch(context, id + "F21", { "sketchPlane" : qUnion([Q0])});
            skLineSegment(sketch, "E134.0.0", {"start": v(-24.25, 9.75) * mm, "end": v(-22, 9.75) * mm});
            skLineSegment(sketch, "E134.0.1", {"start": v(-22, 9.75) * mm, "end": v(-22, 3.25) * mm});
            skLineSegment(sketch, "E134.0.2", {"start": v(-22, 3.25) * mm, "end": v(-24.25, 3.25) * mm});
            skLineSegment(sketch, "E134.0.3", {"start": v(-24.25, 3.25) * mm, "end": v(-24.25, 9.75) * mm});
            skLineSegment(sketch, "E135.0.0", {"start": v(-24.25, -3.25) * mm, "end": v(-22, -3.25) * mm});
            skLineSegment(sketch, "E135.0.1", {"start": v(-22, -3.25) * mm, "end": v(-22, -9.75) * mm});
            skLineSegment(sketch, "E135.0.2", {"start": v(-22, -9.75) * mm, "end": v(-24.25, -9.75) * mm});
            skLineSegment(sketch, "E135.0.3", {"start": v(-24.25, -9.75) * mm, "end": v(-24.25, -3.25) * mm});
            skLineSegment(sketch, "E136", {"start": v(-84, 16.25) * mm, "end": v(-22, 16.25) * mm});
            skLineSegment(sketch, "E137", {"start": v(-84, -16.25) * mm, "end": v(-22, -16.25) * mm});
            skLineSegment(sketch, "E138", {"start": v(-10.25, -10.25) * mm, "end": v(-8.66, -11.84) * mm});
            skLineSegment(sketch, "E139", {"start": v(-8.66, -11.84) * mm, "end": v(-4.07, -7.25) * mm});
            skLineSegment(sketch, "E140", {"start": v(-4.07, -7.25) * mm, "end": v(-5.66, -5.66) * mm});
            skLineSegment(sketch, "E141", {"start": v(-5.66, -5.66) * mm, "end": v(0, 0) * mm});
            skLineSegment(sketch, "E142.1.0", {"start": v(-5.66, 5.66) * mm, "end": v(0, 0) * mm});
            skLineSegment(sketch, "E142.1.1", {"start": v(-7.25, 4.07) * mm, "end": v(-5.66, 5.66) * mm});
            skLineSegment(sketch, "E142.1.2", {"start": v(-10.25, 10.25) * mm, "end": v(-11.84, 8.66) * mm});
            skLineSegment(sketch, "E142.1.3", {"start": v(-11.84, 8.66) * mm, "end": v(-7.25, 4.07) * mm});
            skPoint(sketch, "E142.center", {"position": v(0, 0) * mm});
            skLineSegment(sketch, "E142.anchor1", {"start": v(0, 0) * mm, "end": v(-10.25, -10.25) * mm, "construction": true});
            skLineSegment(sketch, "E142.anchor2", {"start": v(0, 0) * mm, "end": v(-10.25, 10.25) * mm, "construction": true});
            skLineSegment(sketch, "E143", {"start": v(0, 0) * mm, "end": v(-22, 0) * mm, "construction": true});
            skLineSegment(sketch, "E144", {"start": v(-10.25, -10.25) * mm, "end": v(-12.37, -12.37) * mm});
            skLineSegment(sketch, "E145", {"start": v(-12.37, -12.37) * mm, "end": v(-22, -16.25) * mm});
            skLineSegment(sketch, "E146.MirrorCS", {"start": v(-12.37, 12.37) * mm, "end": v(-22, 16.25) * mm});
            skLineSegment(sketch, "E147.MirrorCS", {"start": v(-10.25, 10.25) * mm, "end": v(-12.37, 12.37) * mm});
            skLineSegment(sketch, "E148.0", {"start": v(-86.25, -9.75) * mm, "end": v(-84, -9.75) * mm});
            skLineSegment(sketch, "E149.0", {"start": v(-86.25, -3.25) * mm, "end": v(-84, -3.25) * mm});
            skLineSegment(sketch, "E150.0", {"start": v(-86.25, 3.25) * mm, "end": v(-84, 3.25) * mm});
            skLineSegment(sketch, "E151.0", {"start": v(-86.25, 9.75) * mm, "end": v(-84, 9.75) * mm});
            skLineSegment(sketch, "E152.0", {"start": v(-86.25, 9.75) * mm, "end": v(-86.25, 3.25) * mm});
            skLineSegment(sketch, "E153.0", {"start": v(-86.25, -3.25) * mm, "end": v(-86.25, -9.75) * mm});
            skLineSegment(sketch, "E154.0", {"start": v(-84, 3.25) * mm, "end": v(-84, -3.25) * mm});
            skLineSegment(sketch, "E155", {"start": v(-84, -16.25) * mm, "end": v(-84, -9.75) * mm});
            skLineSegment(sketch, "E156", {"start": v(-84, 9.75) * mm, "end": v(-84, 16.25) * mm});
            skLineSegment(sketch, "E157.bottom", {"start": v(-78, 1.12) * mm, "end": v(-74, 1.12) * mm});
            skLineSegment(sketch, "E157.top", {"start": v(-78, -1.12) * mm, "end": v(-74, -1.13) * mm});
            skLineSegment(sketch, "E157.left", {"start": v(-78, 1.13) * mm, "end": v(-78, -1.13) * mm});
            skLineSegment(sketch, "E157.right", {"start": v(-74, 1.13) * mm, "end": v(-74, -1.13) * mm});
            skLineSegment(sketch, "E158.bottom", {"start": v(-70, 1.12) * mm, "end": v(-66, 1.12) * mm});
            skLineSegment(sketch, "E158.top", {"start": v(-70, -1.13) * mm, "end": v(-66, -1.13) * mm});
            skLineSegment(sketch, "E158.left", {"start": v(-70, 1.13) * mm, "end": v(-70, -1.13) * mm});
            skLineSegment(sketch, "E158.right", {"start": v(-66, 1.12) * mm, "end": v(-66, -1.12) * mm});
            skLineSegment(sketch, "E159", {"start": v(-74, -1.13) * mm, "end": v(-70, -1.13) * mm, "construction": true});
            skLineSegment(sketch, "E160", {"start": v(-78, 0) * mm, "end": v(-82, 0) * mm, "construction": true});
            skPoint(sketch, "E160.endSnap0", {"position": v(-78, 0) * mm});
            skSolve(sketch);
        }
        {
            var Q0;
            Q0=makeQuery(id+"F21.imprint","IMPRINT",FACE,{"disambiguationData":[TD([[makeQuery(id+"F21.imprint","IMPRINT",EDGE,{"derivedFrom":sQuery(id+"F21.wireOp",EDGE,"E134.0.0")}),1.0]])]});
            extrude(context, id + "F22", {"entities" : qUnion([Q0]), "depth" : (getVariable(context, 'ep')) * mm});
        }
        {
            var Q0;
            Q0=makeQuery(id+"F22.opExtrude","SWEPT_FACE",FACE,{"disambiguationData":[OSD([sQuery(id+"F21.wireOp",EDGE,"E157.bottom")])]});
            var sketch = newSketch(context, id + "F23", { "sketchPlane" : qUnion([Q0])});
            skLineSegment(sketch, "E161.0", {"start": v(-78, 2.25) * mm, "end": v(-78, 0) * mm});
            skLineSegment(sketch, "E162.0", {"start": v(-78, 0) * mm, "end": v(-74, 0) * mm});
            skLineSegment(sketch, "E163.0", {"start": v(-74, 2.25) * mm, "end": v(-74, 0) * mm});
            skLineSegment(sketch, "E164.0", {"start": v(-66, 2.25) * mm, "end": v(-66, 0) * mm});
            skLineSegment(sketch, "E165.0", {"start": v(-70, 0) * mm, "end": v(-66, 0) * mm});
            skLineSegment(sketch, "E166.0", {"start": v(-70, 2.25) * mm, "end": v(-70, 0) * mm});
            skLineSegment(sketch, "E167", {"start": v(-78, 2.25) * mm, "end": v(-82, 2.25) * mm});
            skLineSegment(sketch, "E168", {"start": v(-82, 2.25) * mm, "end": v(-82, 6.25) * mm});
            skLineSegment(sketch, "E169", {"start": v(-82, 6.25) * mm, "end": v(-62, 6.25) * mm});
            skLineSegment(sketch, "E170", {"start": v(-62, 6.25) * mm, "end": v(-62, 2.25) * mm});
            skLineSegment(sketch, "E171", {"start": v(-62, 2.25) * mm, "end": v(-66, 2.25) * mm});
            skLineSegment(sketch, "E172", {"start": v(-70, 2.25) * mm, "end": v(-74, 2.25) * mm});
            skSolve(sketch);
        }
        {
            var Q0;
            Q0 = qSketchRegion(id + "F23", true);
            var Q1;
            Q1=makeQuery(id+"F22.opExtrude","SWEPT_FACE",FACE,{"disambiguationData":[OSD([sQuery(id+"F21.wireOp",EDGE,"E157.top")])]});
            extrude(context, id + "F24", {"entities" : qUnion([Q0]), "endBound" : BoundingType.UP_TO_SURFACE, "endBoundEntityFace" : qUnion([Q1]), "depth" : 25 * mm});
        }
        {
            var Q0;
            Q0=makeQuery(id+"F6.opExtrude","SWEPT_BODY",BODY,{"disambiguationData":[OSD([sQuery(id+"F5.wireOp",EDGE,"E26.left"),sQuery(id+"F5.wireOp",EDGE,"E30"),sQuery(id+"F5.wireOp",EDGE,"E31"),sQuery(id+"F5.wireOp",EDGE,"E32")])]});
            var Q1;
            Q1=makeQuery(id+"F22.opExtrude","SWEPT_BODY",BODY,{"disambiguationData":[OSD([sQuery(id+"F21.wireOp",EDGE,"E134.0.0"),sQuery(id+"F21.wireOp",EDGE,"E134.0.1"),sQuery(id+"F21.wireOp",EDGE,"E134.0.2"),sQuery(id+"F21.wireOp",EDGE,"E134.0.3"),sQuery(id+"F21.wireOp",EDGE,"E135.0.0"),sQuery(id+"F21.wireOp",EDGE,"E135.0.1"),sQuery(id+"F21.wireOp",EDGE,"E135.0.2"),sQuery(id+"F21.wireOp",EDGE,"E135.0.3"),sQuery(id+"F21.wireOp",EDGE,"E136"),sQuery(id+"F21.wireOp",EDGE,"E137"),sQuery(id+"F21.wireOp",EDGE,"E138"),sQuery(id+"F21.wireOp",EDGE,"E139"),sQuery(id+"F21.wireOp",EDGE,"E140"),sQuery(id+"F21.wireOp",EDGE,"E141"),sQuery(id+"F21.wireOp",EDGE,"E142.1.0"),sQuery(id+"F21.wireOp",EDGE,"E142.1.1"),sQuery(id+"F21.wireOp",EDGE,"E142.1.2"),sQuery(id+"F21.wireOp",EDGE,"E142.1.3"),sQuery(id+"F21.wireOp",EDGE,"E144"),sQuery(id+"F21.wireOp",EDGE,"E145"),sQuery(id+"F21.wireOp",EDGE,"E146.MirrorCS"),sQuery(id+"F21.wireOp",EDGE,"E147.MirrorCS"),sQuery(id+"F21.wireOp",EDGE,"tspblnoj-Dp5W-AzlG-uek7-DDTLVZN02IB6.right")])]});
            var Q2;
            Q2=makeQuery(id+"F12.opExtrude","SWEPT_BODY",BODY,{"disambiguationData":[OSD([sQuery(id+"F11.wireOp",EDGE,"E50.bottom"),sQuery(id+"F11.wireOp",EDGE,"E50.top"),sQuery(id+"F11.wireOp",EDGE,"E50.left"),sQuery(id+"F11.wireOp",EDGE,"E50.right")])]});
            var Q3;
            Q3=makeQuery(id+"F14.opExtrude","SWEPT_BODY",BODY,{"disambiguationData":[OSD([sQuery(id+"F13.wireOp",EDGE,"E51.0"),sQuery(id+"F13.wireOp",EDGE,"E51.1"),sQuery(id+"F13.wireOp",EDGE,"E51.2"),sQuery(id+"F13.wireOp",EDGE,"E51.3"),sQuery(id+"F13.wireOp",EDGE,"E52.0"),sQuery(id+"F13.wireOp",EDGE,"E52.1"),sQuery(id+"F13.wireOp",EDGE,"E52.2"),sQuery(id+"F13.wireOp",EDGE,"E52.3"),sQuery(id+"F13.wireOp",EDGE,"wZcKvyZ9-swz3-P67m-EJlE-V8fpUGM8ZBwq"),sQuery(id+"F13.wireOp",EDGE,"E53"),sQuery(id+"F13.wireOp",EDGE,"E54.top"),sQuery(id+"F13.wireOp",EDGE,"E54.right"),sQuery(id+"F13.wireOp",EDGE,"E55.bottom"),sQuery(id+"F13.wireOp",EDGE,"E55.top"),sQuery(id+"F13.wireOp",EDGE,"E55.right"),sQuery(id+"F13.wireOp",EDGE,"E56.bottom"),sQuery(id+"F13.wireOp",EDGE,"E56.top"),sQuery(id+"F13.wireOp",EDGE,"E56.right"),sQuery(id+"F13.wireOp",EDGE,"E57.trimOffspring"),sQuery(id+"F13.wireOp",EDGE,"E58.bottom"),sQuery(id+"F13.wireOp",EDGE,"E58.top"),sQuery(id+"F13.wireOp",EDGE,"E58.right"),sQuery(id+"F13.wireOp",EDGE,"E59.bottom"),sQuery(id+"F13.wireOp",EDGE,"E59.top"),sQuery(id+"F13.wireOp",EDGE,"E59.right"),sQuery(id+"F13.wireOp",EDGE,"E60.trimOffspring"),sQuery(id+"F13.wireOp",EDGE,"E61.trimOffspring")])]});
            var Q4;
            Q4=makeQuery(id+"F16.opExtrude","SWEPT_BODY",BODY,{"disambiguationData":[OSD([sQuery(id+"F15.wireOp",EDGE,"E83.0"),sQuery(id+"F15.wireOp",EDGE,"E84.0"),sQuery(id+"F15.wireOp",EDGE,"E85.0"),sQuery(id+"F15.wireOp",EDGE,"E86.0"),sQuery(id+"F15.wireOp",EDGE,"E87.0"),sQuery(id+"F15.wireOp",EDGE,"E88.0"),sQuery(id+"F15.wireOp",EDGE,"E89"),sQuery(id+"F15.wireOp",EDGE,"E90"),sQuery(id+"F15.wireOp",EDGE,"E91"),sQuery(id+"F15.wireOp",EDGE,"E93.MirrorCS"),sQuery(id+"F15.wireOp",EDGE,"E94.MirrorCS"),sQuery(id+"F15.wireOp",EDGE,"E95.MirrorCS"),sQuery(id+"F15.wireOp",EDGE,"E96.MirrorCS"),sQuery(id+"F15.wireOp",EDGE,"E97.MirrorCS"),sQuery(id+"F15.wireOp",EDGE,"E98.MirrorCS"),sQuery(id+"F15.wireOp",EDGE,"E99.MirrorCS"),sQuery(id+"F15.wireOp",EDGE,"E100.MirrorCS"),sQuery(id+"F15.wireOp",EDGE,"E101.MirrorCS"),sQuery(id+"F15.wireOp",EDGE,"E102"),sQuery(id+"F15.wireOp",EDGE,"E103")])]});
            var Q5;
            Q5=makeQuery(id+"F18.opExtrude","SWEPT_BODY",BODY,{"disambiguationData":[OSD([sQuery(id+"F17.wireOp",EDGE,"E110.0"),sQuery(id+"F17.wireOp",EDGE,"E111.0"),sQuery(id+"F17.wireOp",EDGE,"E112.0"),sQuery(id+"F17.wireOp",EDGE,"E113"),sQuery(id+"F17.wireOp",EDGE,"E114"),sQuery(id+"F17.wireOp",EDGE,"E115"),sQuery(id+"F17.wireOp",EDGE,"E116"),sQuery(id+"F17.wireOp",EDGE,"E117"),sQuery(id+"F17.wireOp",EDGE,"E118"),sQuery(id+"F17.wireOp",EDGE,"E119"),sQuery(id+"F17.wireOp",EDGE,"E120"),sQuery(id+"F17.wireOp",EDGE,"E121")])]});
            var Q6;
            Q6=makeQuery(id+"F20.opExtrude","SWEPT_BODY",BODY,{"disambiguationData":[OSD([sQuery(id+"F19.wireOp",EDGE,"E122.0"),sQuery(id+"F19.wireOp",EDGE,"E123.0"),sQuery(id+"F19.wireOp",EDGE,"E124.0"),sQuery(id+"F19.wireOp",EDGE,"E125.0"),sQuery(id+"F19.wireOp",EDGE,"E126.0"),sQuery(id+"F19.wireOp",EDGE,"E127.0"),sQuery(id+"F19.wireOp",EDGE,"E128.0"),sQuery(id+"F19.wireOp",EDGE,"E129.0"),sQuery(id+"F19.wireOp",EDGE,"E130"),sQuery(id+"F19.wireOp",EDGE,"E131"),sQuery(id+"F19.wireOp",EDGE,"E132"),sQuery(id+"F19.wireOp",EDGE,"E133")])]});
            var Q7;
            Q7=makeQuery(id+"F24.opExtrude","SWEPT_BODY",BODY,{"disambiguationData":[OSD([sQuery(id+"F23.wireOp",EDGE,"E161.0"),sQuery(id+"F23.wireOp",EDGE,"E162.0"),sQuery(id+"F23.wireOp",EDGE,"E163.0"),sQuery(id+"F23.wireOp",EDGE,"E164.0"),sQuery(id+"F23.wireOp",EDGE,"E165.0"),sQuery(id+"F23.wireOp",EDGE,"E166.0"),sQuery(id+"F23.wireOp",EDGE,"E167"),sQuery(id+"F23.wireOp",EDGE,"E168"),sQuery(id+"F23.wireOp",EDGE,"E169"),sQuery(id+"F23.wireOp",EDGE,"E170"),sQuery(id+"F23.wireOp",EDGE,"E171"),sQuery(id+"F23.wireOp",EDGE,"E172")])]});
            var Q8;
            Q8=sQuery(id+"F1.wireOp",EDGE,"E17");
            circularPattern(context, id + "F25", {"entities" : qUnion([Q0, Q1, Q2, Q3, Q4, Q5, Q6, Q7]), "axis" : qUnion([Q8]), "angle" : 360 * degree, "instanceCount" : 4, "equalSpace" : true});
        }
    });
